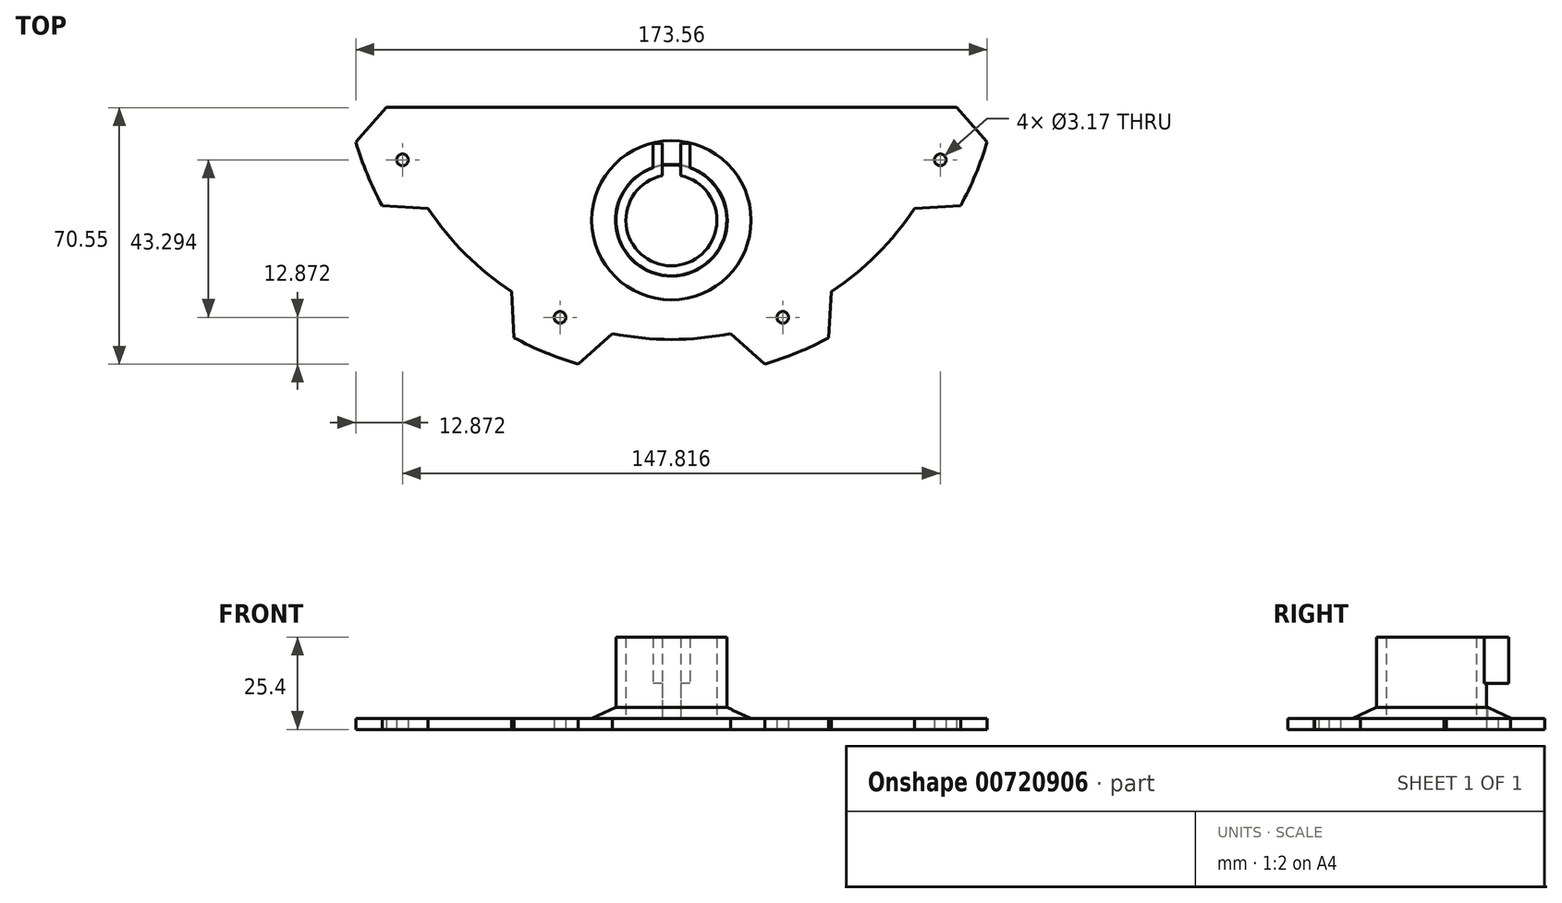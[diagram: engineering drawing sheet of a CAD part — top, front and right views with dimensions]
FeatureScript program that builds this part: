
annotation { "Feature Type Name" : "Feature", "Feature Type Description" : "" }
export const myFeature = defineFeature(function(context is Context, id is Id, definition is map)
    precondition{}
    {
        {
            var Q0;
            Q0=qCreatedBy(makeId("Top.planeOp"),FACE);
            var sketch = newSketch(context, id + "F0", { "sketchPlane" : qUnion([Q0])});
            skCircle(sketch, "E0", {"center": v(0, -47.22) * mm, "radius": 15.24 * mm});
            skCircle(sketch, "E1", {"center": v(0, -47.22) * mm, "radius": 12.5 * mm});
            skCircle(sketch, "E2", {"center": v(0, -47.22) * mm, "radius": 22.23 * mm});
            skLineSegment(sketch, "E3.0", {"start": v(2.54, -34.97) * mm, "end": v(2.54, -26.1) * mm});
            skLineSegment(sketch, "E4.0", {"start": v(-2.54, -34.97) * mm, "end": v(-2.54, -26.1) * mm});
            skLineSegment(sketch, "E5.0", {"start": v(5.08, -32.85) * mm, "end": v(5.08, -26.1) * mm});
            skLineSegment(sketch, "E6.0", {"start": v(-5.08, -32.85) * mm, "end": v(-5.08, -26.1) * mm});
            skLineSegment(sketch, "E7", {"start": v(5.08, -26.1) * mm, "end": v(2.54, -26.1) * mm});
            skLineSegment(sketch, "E8.trimOffspring", {"start": v(-2.54, -26.1) * mm, "end": v(-5.08, -26.1) * mm});
            skArc(sketch, "E9", {"start": v(-86.78, -25.64) * mm, "mid": v(-83.6, -34.63) * mm, "end": v(-79.5, -43.24) * mm});
            skCircle(sketch, "E10", {"center": v(73.9, -30.61) * mm, "radius": 1.59 * mm});
            skCircle(sketch, "E11", {"center": v(-30.61, -73.9) * mm, "radius": 1.59 * mm});
            skCircle(sketch, "E12", {"center": v(-73.9, -30.61) * mm, "radius": 1.59 * mm});
            skCircle(sketch, "E13", {"center": v(30.61, -73.9) * mm, "radius": 1.59 * mm});
            skArc(sketch, "E14.trimOffspring", {"start": v(-43.24, -79.5) * mm, "mid": v(-34.63, -83.6) * mm, "end": v(-25.64, -86.78) * mm});
            skArc(sketch, "E15.trimOffspring", {"start": v(25.64, -86.78) * mm, "mid": v(34.63, -83.6) * mm, "end": v(43.24, -79.5) * mm});
            skArc(sketch, "E16.trimOffspring", {"start": v(79.5, -43.24) * mm, "mid": v(83.6, -34.63) * mm, "end": v(86.78, -25.64) * mm});
            skLineSegment(sketch, "E17", {"start": v(-86.78, -25.64) * mm, "end": v(-78.33, -16.23) * mm});
            skLineSegment(sketch, "E18", {"start": v(-79.5, -43.24) * mm, "end": v(-66.86, -43.92) * mm});
            skLineSegment(sketch, "E19", {"start": v(-43.92, -66.86) * mm, "end": v(-43.24, -79.5) * mm});
            skLineSegment(sketch, "E20", {"start": v(-16.23, -78.33) * mm, "end": v(-25.64, -86.78) * mm});
            skLineSegment(sketch, "E21", {"start": v(16.23, -78.33) * mm, "end": v(25.64, -86.78) * mm});
            skLineSegment(sketch, "E22", {"start": v(43.92, -66.86) * mm, "end": v(43.24, -79.5) * mm});
            skLineSegment(sketch, "E23", {"start": v(66.86, -43.92) * mm, "end": v(79.5, -43.24) * mm});
            skLineSegment(sketch, "E24", {"start": v(78.33, -16.23) * mm, "end": v(86.78, -25.64) * mm});
            skLineSegment(sketch, "E25", {"start": v(-78.33, -16.23) * mm, "end": v(78.33, -16.23) * mm});
            skArc(sketch, "E26.trimOffspring", {"start": v(-66.86, -43.92) * mm, "mid": v(-56.57, -56.57) * mm, "end": v(-43.92, -66.86) * mm});
            skArc(sketch, "E27.trimOffspring", {"start": v(-16.23, -78.33) * mm, "mid": v(0, -80) * mm, "end": v(16.23, -78.33) * mm});
            skArc(sketch, "E28.trimOffspring", {"start": v(43.92, -66.86) * mm, "mid": v(56.57, -56.57) * mm, "end": v(66.86, -43.92) * mm});
            skPoint(sketch, "E29.orphan", {"position": v(-2.54, -32.2) * mm});
            skPoint(sketch, "E30.orphan", {"position": v(2.54, -32.2) * mm});
            skSolve(sketch);
        }
        {
            var Q0;
            Q0=makeQuery(id+"F0.imprint","IMPRINT",FACE,{"disambiguationData":[TD([[makeQuery(id+"F0.imprint","IMPRINT",EDGE,{"derivedFrom":sQuery(id+"F0.wireOp",EDGE,"E2")}),-1.0]])]});
            var Q1;
            Q1=makeQuery(id+"F0.imprint","IMPRINT",FACE,{"disambiguationData":[TD([[makeQuery(id+"F0.imprint","IMPRINT",EDGE,{"derivedFrom":sQuery(id+"F0.wireOp",EDGE,"E2")}),1.0]])]});
            var Q2;
            {var subQ0=sQuery(id+"F0.wireOp",EDGE,"E3.0");Q2=makeQuery(id+"F0.imprint","IMPRINT",FACE,{"disambiguationData":[TD([[makeQuery(id+"F0.imprint","IMPRINT",EDGE,{"derivedFrom":subQ0}),-1.0]])]});}
            var Q3;
            {var subQ0=sQuery(id+"F0.wireOp",EDGE,"E4.0");Q3=makeQuery(id+"F0.imprint","IMPRINT",FACE,{"disambiguationData":[TD([[makeQuery(id+"F0.imprint","IMPRINT",EDGE,{"derivedFrom":subQ0}),1.0]])]});}
            var Q4;
            Q4=makeQuery(id+"F0.imprint","IMPRINT",FACE,{"disambiguationData":[TD([[makeQuery(id+"F0.imprint","IMPRINT",EDGE,{"derivedFrom":sQuery(id+"F0.wireOp",EDGE,"E1")}),-1.0]])]});
            var Q5;
            Q5=makeQuery(id+"F0.imprint","IMPRINT",FACE,{"disambiguationData":[TD([[makeQuery(id+"F0.imprint","IMPRINT",EDGE,{"derivedFrom":sQuery(id+"F0.wireOp",EDGE,"E1")}),1.0]])]});
            extrude(context, id + "F1", {"entities" : qUnion([Q0, Q1, Q2, Q3, Q4, Q5]), "depth" : 3 * mm, "offsetDistance" : 25.4 * mm});
        }
        {
            var Q0;
            {var subQ0=sQuery(id+"F0.wireOp",EDGE,"E0");var subQ1=makeQuery(id+"F0.imprint","INTERSECT",VERTEX,{"derivedFrom":[subQ0,sQuery(id+"F0.wireOp",EDGE,"E5.0")]});Q0=makeQuery(id+"F0.imprint","IMPRINT",FACE,{"disambiguationData":[TD([[makeQuery(id+"F0.imprint","IMPRINT",EDGE,{"disambiguationData":[TD([[subQ1,-1.0]])],"derivedFrom":subQ0}),1.0]])]});}
            extrude(context, id + "F2", {"entities" : qUnion([Q0]), "operationType" : NewBodyOperationType.ADD, "depth" : 25.4 * mm, "offsetDistance" : 25.4 * mm});
        }
        {
            var Q0;
            {var subQ0=sQuery(id+"F0.wireOp",EDGE,"E5.0");Q0=makeQuery(id+"F0.imprint","IMPRINT",FACE,{"disambiguationData":[TD([[makeQuery(id+"F0.imprint","IMPRINT",EDGE,{"derivedFrom":subQ0}),1.0]])]});}
            var Q1;
            {var subQ0=sQuery(id+"F0.wireOp",EDGE,"E6.0");Q1=makeQuery(id+"F0.imprint","IMPRINT",FACE,{"disambiguationData":[TD([[makeQuery(id+"F0.imprint","IMPRINT",EDGE,{"derivedFrom":subQ0}),-1.0]])]});}
            extrude(context, id + "F3", {"entities" : qUnion([Q0, Q1]), "operationType" : NewBodyOperationType.ADD, "depth" : 25.4 * mm, "offsetDistance" : 25.4 * mm});
        }
        {
            var Q0;
            {var subQ0=sQuery(id+"F0.wireOp",EDGE,"E5.0");Q0=makeQuery(id+"F0.imprint","IMPRINT",FACE,{"disambiguationData":[TD([[makeQuery(id+"F0.imprint","IMPRINT",EDGE,{"derivedFrom":subQ0}),1.0]])]});}
            var Q1;
            {var subQ0=sQuery(id+"F0.wireOp",EDGE,"E6.0");Q1=makeQuery(id+"F0.imprint","IMPRINT",FACE,{"disambiguationData":[TD([[makeQuery(id+"F0.imprint","IMPRINT",EDGE,{"derivedFrom":subQ0}),-1.0]])]});}
            extrude(context, id + "F4", {"entities" : qUnion([Q0, Q1]), "operationType" : NewBodyOperationType.REMOVE, "depth" : 12.7 * mm, "offsetDistance" : 25.4 * mm});
        }
        {
            var Q0;
            {var subQ0=sQuery(id+"F0.wireOp",EDGE,"E5.0");Q0=makeQuery(id+"F0.imprint","IMPRINT",FACE,{"disambiguationData":[TD([[makeQuery(id+"F0.imprint","IMPRINT",EDGE,{"derivedFrom":subQ0}),1.0]])]});}
            var Q1;
            {var subQ0=sQuery(id+"F0.wireOp",EDGE,"E6.0");Q1=makeQuery(id+"F0.imprint","IMPRINT",FACE,{"disambiguationData":[TD([[makeQuery(id+"F0.imprint","IMPRINT",EDGE,{"derivedFrom":subQ0}),-1.0]])]});}
            extrude(context, id + "F5", {"entities" : qUnion([Q0, Q1]), "operationType" : NewBodyOperationType.ADD, "depth" : 3 * mm, "offsetDistance" : 25.4 * mm});
        }
        {
            var Q0;
            Q0=makeQuery(id+"F0.imprint","IMPRINT",FACE,{"disambiguationData":[TD([[makeQuery(id+"F0.imprint","IMPRINT",EDGE,{"derivedFrom":sQuery(id+"F0.wireOp",EDGE,"E2")}),1.0]])]});
            var Q1;
            {var subQ0=sQuery(id+"F0.wireOp",EDGE,"E5.0");Q1=makeQuery(id+"F0.imprint","IMPRINT",FACE,{"disambiguationData":[TD([[makeQuery(id+"F0.imprint","IMPRINT",EDGE,{"derivedFrom":subQ0}),1.0]])]});}
            var Q2;
            {var subQ0=sQuery(id+"F0.wireOp",EDGE,"E6.0");Q2=makeQuery(id+"F0.imprint","IMPRINT",FACE,{"disambiguationData":[TD([[makeQuery(id+"F0.imprint","IMPRINT",EDGE,{"derivedFrom":subQ0}),-1.0]])]});}
            extrude(context, id + "F6", {"entities" : qUnion([Q0, Q1, Q2]), "operationType" : NewBodyOperationType.ADD, "depth" : 6 * mm, "offsetDistance" : 25.4 * mm});
        }
        {
            var Q0;
            Q0=makeQuery(id+"F6.opExtrude","CAP_EDGE",EDGE,{"disambiguationData":[OSD([sQuery(id+"F0.wireOp",EDGE,"E2")])],"isStart":false});
            chamfer(context, id + "F7", {"entities" : qUnion([Q0]), "chamferType" : ChamferType.TWO_OFFSETS, "width1" : 6.86 * mm, "oppositeDirection" : false, "width2" : 3.15 * mm, "tangentPropagation" : true});
        }
    });
